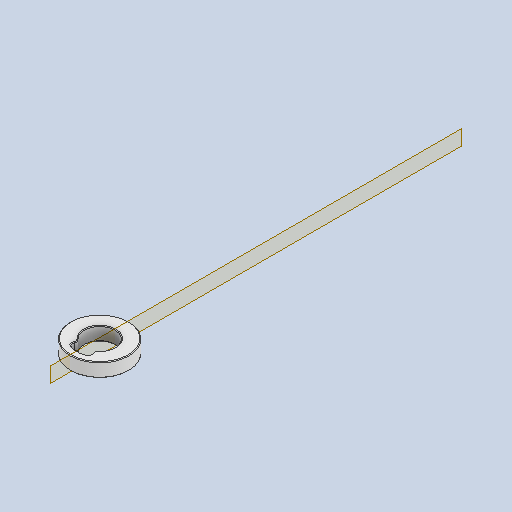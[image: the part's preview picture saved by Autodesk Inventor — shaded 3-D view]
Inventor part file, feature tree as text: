
AUTODESK INVENTOR PART (.ipt)
format: ipt  version: 2022 (Build 260153000, 153)  size: 163,840 bytes
history: native  units: in
note: dims shown in document units (in); Inventor stores cm internally (conversion verified against a paired STEP export)
features: sketch x1, other x1, plane x1, projected_geometry x1
ambient origin geometry x8: Origin, YZ Plane, XZ Plane, XY Plane, X Axis, Y Axis, Z Axis, Center Point
bodies: Solid1 (feature_tree), Body1 (feature_tree)
feature tree (4):
  sketch  "Sketch1"  dims[d0=90.0deg]
  other  "Work Axis1"
  plane  "Work Plane1"
  projected_geometry  "Projected Loop1"
